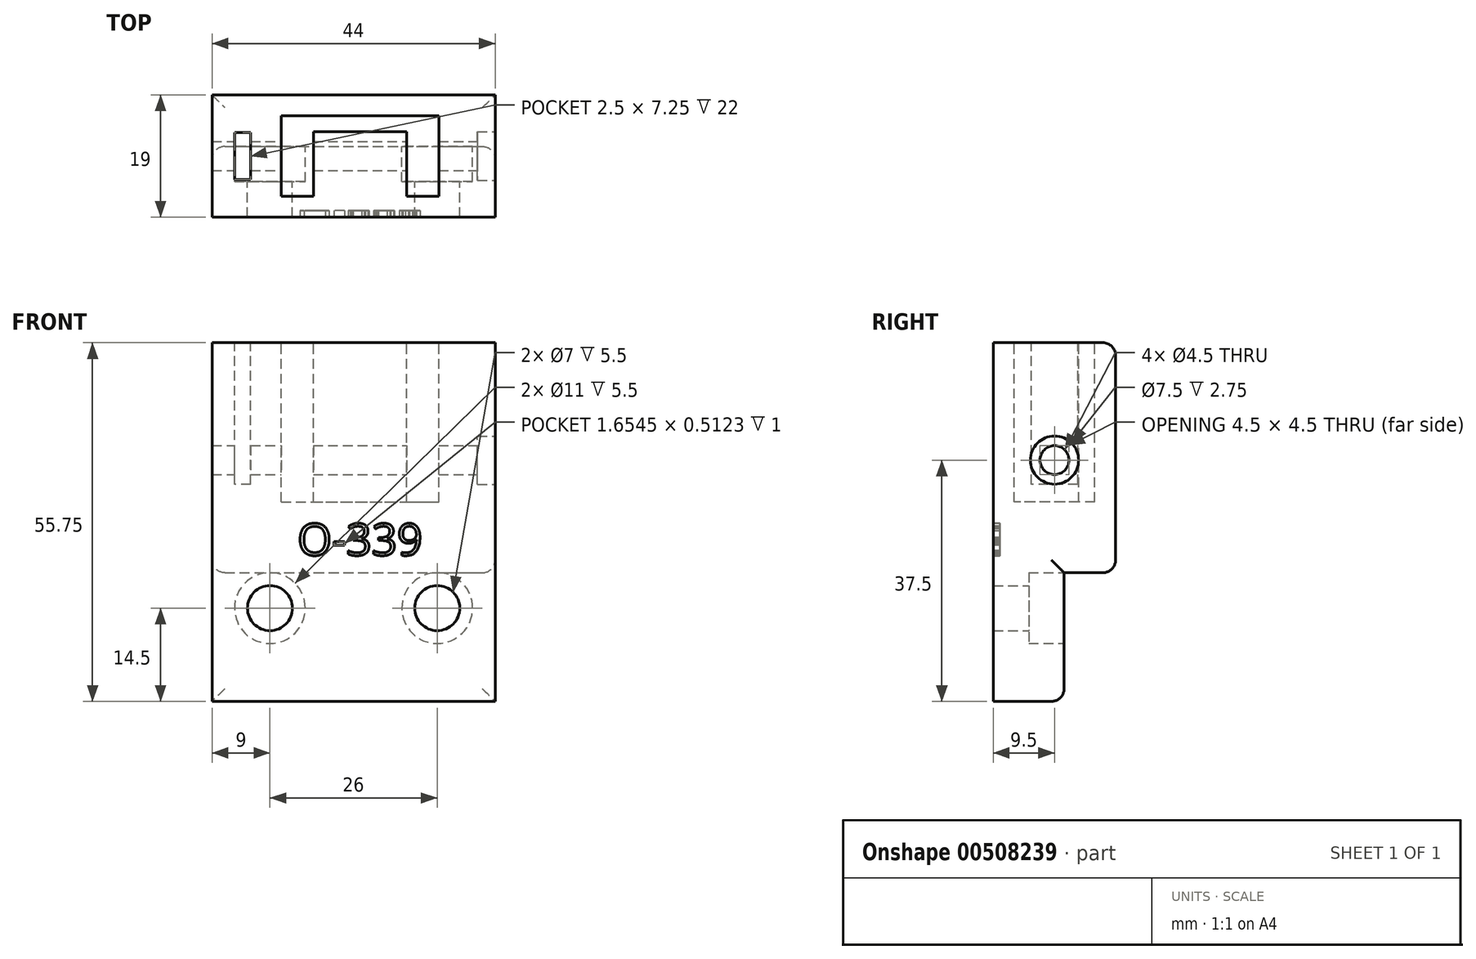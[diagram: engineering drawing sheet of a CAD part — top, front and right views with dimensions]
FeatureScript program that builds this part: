
annotation { "Feature Type Name" : "Feature", "Feature Type Description" : "" }
export const myFeature = defineFeature(function(context is Context, id is Id, definition is map)
    precondition{}
    {
        {
            var Q0;
            Q0=qCreatedBy(makeId("Top.planeOp"),FACE);
            var sketch = newSketch(context, id + "F0", { "sketchPlane" : qUnion([Q0])});
            skLineSegment(sketch, "E0.bottom", {"start": v(-29, 9.5) * mm, "end": v(29, 9.5) * mm});
            skLineSegment(sketch, "E0.top", {"start": v(-29, -9.5) * mm, "end": v(29, -9.5) * mm});
            skLineSegment(sketch, "E0.left", {"start": v(-29, 9.5) * mm, "end": v(-29, -9.5) * mm});
            skLineSegment(sketch, "E0.right", {"start": v(29, 9.5) * mm, "end": v(29, -9.5) * mm});
            skSolve(sketch);
        }
        {
            var Q0;
            Q0=qSketchRegion(id+"F0",true);
            extrude(context, id + "F1", {"entities" : qUnion([Q0]), "depth" : 11 * mm});
        }
        {
            var Q0;
            Q0=makeQuery(id+"F1.opExtrude","CAP_FACE",FACE,{"disambiguationData":[OSD([sQuery(id+"F0.wireOp",EDGE,"E0.bottom"),sQuery(id+"F0.wireOp",EDGE,"E0.top"),sQuery(id+"F0.wireOp",EDGE,"E0.left"),sQuery(id+"F0.wireOp",EDGE,"E0.right"),sQuery(id+"F0.wireOp",EDGE,"AuSHMrTt-jpj0-5Ru2-xaIe-a4Oixfi13iDE"),sQuery(id+"F0.wireOp",EDGE,"9J5HWsQ0-lQpk-E1t6-wWkI-SOKKZm0BYfsw"),sQuery(id+"F0.wireOp",EDGE,"2GzKSPJo-uI2N-Esed-kJXd-WJqO7sIm6bVz"),sQuery(id+"F0.wireOp",EDGE,"DJKESrdY-mQTo-sUHj-6MfV-pHmhVGQO2tIG")])],"isStart":false});
            var sketch = newSketch(context, id + "F2", { "sketchPlane" : qUnion([Q0])});
            skLineSegment(sketch, "E1.bottom", {"start": v(-29, 9.5) * mm, "end": v(29, 9.5) * mm});
            skLineSegment(sketch, "E1.top", {"start": v(-29, -9.5) * mm, "end": v(29, -9.5) * mm});
            skLineSegment(sketch, "E1.left", {"start": v(-29, 9.5) * mm, "end": v(-29, -9.5) * mm});
            skLineSegment(sketch, "E1.right", {"start": v(29, 9.5) * mm, "end": v(29, -9.5) * mm});
            skPoint(sketch, "E1.middle", {"position": v(0, 0) * mm});
            skSolve(sketch);
        }
        {
            var Q0;
            Q0=qSketchRegion(id+"F2",true);
            extrude(context, id + "F3", {"entities" : qUnion([Q0]), "operationType" : NewBodyOperationType.ADD, "depth" : 24.75 * mm});
        }
        {
            var Q0;
            Q0=makeQuery(id+"F3.opExtrude","CAP_FACE",FACE,{"disambiguationData":[OSD([sQuery(id+"F2.wireOp",EDGE,"E1.bottom"),sQuery(id+"F2.wireOp",EDGE,"E1.top"),sQuery(id+"F2.wireOp",EDGE,"E1.left"),sQuery(id+"F2.wireOp",EDGE,"E1.right")])],"isStart":false});
            var sketch = newSketch(context, id + "F4", { "sketchPlane" : qUnion([Q0])});
            skLineSegment(sketch, "E2.bottom", {"start": v(-12.25, 6.25) * mm, "end": v(-7.25, 6.25) * mm});
            skLineSegment(sketch, "E2.top", {"start": v(-12.25, -6.25) * mm, "end": v(-7.25, -6.25) * mm});
            skLineSegment(sketch, "E2.left", {"start": v(-12.25, 6.25) * mm, "end": v(-12.25, -6.25) * mm});
            skLineSegment(sketch, "E2.right", {"start": v(-7.25, 6.25) * mm, "end": v(-7.25, -6.25) * mm});
            skPoint(sketch, "E2.middle", {"position": v(-9.75, 0) * mm});
            skLineSegment(sketch, "E3.bottom", {"start": v(7.25, 6.25) * mm, "end": v(12.25, 6.25) * mm});
            skLineSegment(sketch, "E3.top", {"start": v(7.25, -6.25) * mm, "end": v(12.25, -6.25) * mm});
            skLineSegment(sketch, "E3.left", {"start": v(7.25, 6.25) * mm, "end": v(7.25, -6.25) * mm});
            skLineSegment(sketch, "E3.right", {"start": v(12.25, 6.25) * mm, "end": v(12.25, -6.25) * mm});
            skPoint(sketch, "E3.middle", {"position": v(9.75, 0) * mm});
            skSolve(sketch);
        }
        {
            var Q0;
            Q0=qSketchRegion(id+"F4",true);
            extrude(context, id + "F5", {"entities" : qUnion([Q0]), "operationType" : NewBodyOperationType.REMOVE, "oppositeDirection" : true, "depth" : 24.75 * mm});
        }
        {
            var Q0;
            Q0=makeQuery(id+"F3.boolean.opBoolean","MERGE",FACE,{"derivedFrom":[makeQuery(id+"F1.opExtrude","SWEPT_FACE",FACE,{"disambiguationData":[OSD([sQuery(id+"F0.wireOp",EDGE,"E0.right")])]}),makeQuery(id+"F3.opExtrude","SWEPT_FACE",FACE,{"disambiguationData":[OSD([sQuery(id+"F2.wireOp",EDGE,"E1.right")])]})]});
            var sketch = newSketch(context, id + "F6", { "sketchPlane" : qUnion([Q0])});
            skCircle(sketch, "E4", {"center": v(0, 17.5) * mm, "radius": 2.25 * mm});
            skSolve(sketch);
        }
        {
            var Q0;
            Q0=qSketchRegion(id+"F6",true);
            extrude(context, id + "F7", {"entities" : qUnion([Q0]), "operationType" : NewBodyOperationType.REMOVE, "endBound" : BoundingType.THROUGH_ALL, "oppositeDirection" : true, "depth" : 53 * mm});
        }
        {
            var Q0;
            Q0=makeQuery(id+"F3.opExtrude","CAP_FACE",FACE,{"disambiguationData":[OSD([sQuery(id+"F2.wireOp",EDGE,"E1.bottom"),sQuery(id+"F2.wireOp",EDGE,"E1.top"),sQuery(id+"F2.wireOp",EDGE,"E1.left"),sQuery(id+"F2.wireOp",EDGE,"E1.right")])],"isStart":false});
            var sketch = newSketch(context, id + "F8", { "sketchPlane" : qUnion([Q0])});
            skLineSegment(sketch, "E5.bottom", {"start": v(-7.25, 6.25) * mm, "end": v(7.25, 6.25) * mm});
            skLineSegment(sketch, "E5.top", {"start": v(-7.25, 3.75) * mm, "end": v(7.25, 3.75) * mm});
            skLineSegment(sketch, "E5.left", {"start": v(-7.25, 6.25) * mm, "end": v(-7.25, 3.75) * mm});
            skLineSegment(sketch, "E5.right", {"start": v(7.25, 6.25) * mm, "end": v(7.25, 3.75) * mm});
            skSolve(sketch);
        }
        {
            var Q0;
            Q0=qSketchRegion(id+"F8",true);
            extrude(context, id + "F9", {"entities" : qUnion([Q0]), "operationType" : NewBodyOperationType.REMOVE, "oppositeDirection" : true, "depth" : 24.75 * mm});
        }
        {
            var Q0;
            Q0=makeQuery(id+"F3.boolean.opBoolean","MERGE",FACE,{"derivedFrom":[makeQuery(id+"F1.opExtrude","SWEPT_FACE",FACE,{"disambiguationData":[OSD([sQuery(id+"F0.wireOp",EDGE,"E0.right")])]}),makeQuery(id+"F3.opExtrude","SWEPT_FACE",FACE,{"disambiguationData":[OSD([sQuery(id+"F2.wireOp",EDGE,"E1.right")])]})]});
            var sketch = newSketch(context, id + "F10", { "sketchPlane" : qUnion([Q0])});
            skCircle(sketch, "E6", {"center": v(0, 17.5) * mm, "radius": 3.75 * mm});
            skSolve(sketch);
        }
        {
            var Q0;
            Q0=qSketchRegion(id+"F10",true);
            extrude(context, id + "F11", {"entities" : qUnion([Q0]), "operationType" : NewBodyOperationType.REMOVE, "oppositeDirection" : true, "depth" : 10.75 * mm});
        }
        {
            var Q0;
            Q0=makeQuery(id+"F3.opExtrude","CAP_FACE",FACE,{"disambiguationData":[OSD([sQuery(id+"F2.wireOp",EDGE,"E1.bottom"),sQuery(id+"F2.wireOp",EDGE,"E1.top"),sQuery(id+"F2.wireOp",EDGE,"E1.left"),sQuery(id+"F2.wireOp",EDGE,"E1.right")])],"isStart":false});
            var sketch = newSketch(context, id + "F12", { "sketchPlane" : qUnion([Q0])});
            skLineSegment(sketch, "E7.bottom", {"start": v(-17, 3.63) * mm, "end": v(-19.5, 3.63) * mm});
            skLineSegment(sketch, "E7.top", {"start": v(-17, -3.62) * mm, "end": v(-19.5, -3.62) * mm});
            skLineSegment(sketch, "E7.left", {"start": v(-17, 3.63) * mm, "end": v(-17, -3.62) * mm});
            skLineSegment(sketch, "E7.right", {"start": v(-19.5, 3.63) * mm, "end": v(-19.5, -3.62) * mm});
            skPoint(sketch, "E7.middle", {"position": v(-18.25, 0) * mm});
            skSolve(sketch);
        }
        {
            var Q0;
            Q0=qSketchRegion(id+"F12",true);
            extrude(context, id + "F13", {"entities" : qUnion([Q0]), "operationType" : NewBodyOperationType.REMOVE, "oppositeDirection" : true, "depth" : 22 * mm});
        }
        {
            var Q0;
            Q0=makeQuery(id+"F1.opExtrude","SWEPT_FACE",FACE,{"disambiguationData":[OSD([sQuery(id+"F0.wireOp",EDGE,"E0.top")])]});
            var sketch = newSketch(context, id + "F14", { "sketchPlane" : qUnion([Q0])});
            skText(sketch, "E8", { "text": "O-339", "fontName": "OpenSans-Regular.ttf"});
            const initialGuessF14  = {"E8": [-0.00974, 0.0027, 1, 0, 0.00497]};
            skSetInitialGuess(sketch, initialGuessF14);
            skSolve(sketch);
        }
        {
            var Q0;
            Q0=qSketchRegion(id+"F14",true);
            extrude(context, id + "F15", {"entities" : qUnion([Q0]), "operationType" : NewBodyOperationType.REMOVE, "oppositeDirection" : true, "depth" : 1 * mm});
        }
        {
            var Q0;
            {var subQ1=sQuery(id+"F0.wireOp",EDGE,"E0.left");var subQ2=sQuery(id+"F0.wireOp",EDGE,"E0.top");var subQ5=sQuery(id+"F2.wireOp",EDGE,"E1.top");Q0=makeQuery(id+"FO3PEAp2ygwaakO_1.boolean.opBoolean","MERGE",FACE,{"derivedFrom":[makeQuery(id+"F15.boolean.opBoolean","SPLIT",FACE,{"disambiguationData":[TD([makeQuery(id+"F1.opExtrude","SWEPT_FACE",FACE,{"disambiguationData":[OSD([subQ1])]})])],"derivedFrom":makeQuery(id+"F3.boolean.opBoolean","MERGE",FACE,{"derivedFrom":[makeQuery(id+"F1.opExtrude","SWEPT_FACE",FACE,{"disambiguationData":[OSD([subQ2])]}),makeQuery(id+"F3.opExtrude","SWEPT_FACE",FACE,{"disambiguationData":[OSD([subQ5])]})]})}),makeQuery(id+"FO3PEAp2ygwaakO_1.opExtrude","SWEPT_FACE",FACE,{"disambiguationData":[OSD([sQuery(id+"F4FtiOInvpE9sW0_1.wireOp",EDGE,"hhqaLyYQ-Ikl1-l38m-BBv7-oSqBDNAxtoTe")])]})]});}
            var sketch = newSketch(context, id + "F16", { "sketchPlane" : qUnion([Q0])});
            skLineSegment(sketch, "E9.bottom", {"start": v(-29, 0) * mm, "end": v(29, 0) * mm});
            skLineSegment(sketch, "E9.top", {"start": v(-29, -20) * mm, "end": v(29, -20) * mm});
            skLineSegment(sketch, "E9.left", {"start": v(-29, 0) * mm, "end": v(-29, -20) * mm});
            skLineSegment(sketch, "E9.right", {"start": v(29, 0) * mm, "end": v(29, -20) * mm});
            skSolve(sketch);
        }
        {
            var Q0;
            Q0=qSketchRegion(id+"F16",true);
            extrude(context, id + "F17", {"entities" : qUnion([Q0]), "operationType" : NewBodyOperationType.ADD, "oppositeDirection" : true, "depth" : 11 * mm});
        }
        {
            var Q0;
            Q0=makeQuery(id+"F17.opExtrude","CAP_FACE",FACE,{"disambiguationData":[OSD([sQuery(id+"F16.wireOp",EDGE,"E9.bottom"),sQuery(id+"F16.wireOp",EDGE,"E9.top"),sQuery(id+"F16.wireOp",EDGE,"E9.left"),sQuery(id+"F16.wireOp",EDGE,"E9.right")])],"isStart":false});
            var sketch = newSketch(context, id + "F18", { "sketchPlane" : qUnion([Q0])});
            skCircle(sketch, "E10", {"center": v(-12, -5.5) * mm, "radius": 3.5 * mm});
            skCircle(sketch, "E11", {"center": v(14, -5.5) * mm, "radius": 3.5 * mm});
            skSolve(sketch);
        }
        {
            var Q0;
            Q0=qSketchRegion(id+"F18",true);
            extrude(context, id + "F19", {"entities" : qUnion([Q0]), "operationType" : NewBodyOperationType.REMOVE, "endBound" : BoundingType.THROUGH_ALL, "oppositeDirection" : true, "depth" : 25 * mm});
        }
        {
            var Q0;
            Q0=makeQuery(id+"F17.opExtrude","CAP_FACE",FACE,{"disambiguationData":[OSD([sQuery(id+"F16.wireOp",EDGE,"E9.bottom"),sQuery(id+"F16.wireOp",EDGE,"E9.top"),sQuery(id+"F16.wireOp",EDGE,"E9.left"),sQuery(id+"F16.wireOp",EDGE,"E9.right")])],"isStart":false});
            var sketch = newSketch(context, id + "F20", { "sketchPlane" : qUnion([Q0])});
            skCircle(sketch, "E12", {"center": v(-12, -5.5) * mm, "radius": 5.5 * mm});
            skCircle(sketch, "E13", {"center": v(14, -5.5) * mm, "radius": 5.5 * mm});
            skSolve(sketch);
        }
        {
            var Q0;
            Q0=qSketchRegion(id+"F20",true);
            extrude(context, id + "F21", {"entities" : qUnion([Q0]), "operationType" : NewBodyOperationType.REMOVE, "oppositeDirection" : true, "depth" : 5.5 * mm});
        }
        {
            var Q0;
            Q0=makeQuery(id+"F3.boolean.opBoolean","MERGE",FACE,{"derivedFrom":[makeQuery(id+"F1.opExtrude","SWEPT_FACE",FACE,{"disambiguationData":[OSD([sQuery(id+"F0.wireOp",EDGE,"E0.bottom")])]}),makeQuery(id+"F3.opExtrude","SWEPT_FACE",FACE,{"disambiguationData":[OSD([sQuery(id+"F2.wireOp",EDGE,"E1.bottom")])]})]});
            var sketch = newSketch(context, id + "F22", { "sketchPlane" : qUnion([Q0])});
            skLineSegment(sketch, "E14.bottom", {"start": v(-29, 35.75) * mm, "end": v(-21, 35.75) * mm});
            skLineSegment(sketch, "E14.top", {"start": v(-29, -20) * mm, "end": v(-21, -20) * mm});
            skLineSegment(sketch, "E14.left", {"start": v(-29, 35.75) * mm, "end": v(-29, -20) * mm});
            skLineSegment(sketch, "E15.bottom", {"start": v(29, 35.75) * mm, "end": v(23, 35.75) * mm});
            skLineSegment(sketch, "E15.top", {"start": v(29, -20) * mm, "end": v(23, -20) * mm});
            skLineSegment(sketch, "E15.left", {"start": v(29, 35.75) * mm, "end": v(29, -20) * mm});
            skLineSegment(sketch, "E15.right", {"start": v(23, 35.75) * mm, "end": v(23, -20) * mm});
            skLineSegment(sketch, "E16", {"start": v(-21, 35.75) * mm, "end": v(-21, -20) * mm});
            skSolve(sketch);
        }
        {
            var Q0;
            Q0 = qSketchRegion(id + "F22", true);
            extrude(context, id + "F23", {"entities" : qUnion([Q0]), "operationType" : NewBodyOperationType.REMOVE, "endBound" : BoundingType.THROUGH_ALL, "oppositeDirection" : true, "depth" : 25 * mm});
        }
        {
            var Q0;
            Q0=makeQuery(id+"F23.boolean.opBoolean","INTERSECT",EDGE,{"derivedFrom":[makeQuery(id+"F17.opExtrude","CAP_FACE",FACE,{"disambiguationData":[OSD([sQuery(id+"F16.wireOp",EDGE,"E9.bottom"),sQuery(id+"F16.wireOp",EDGE,"E9.top"),sQuery(id+"F16.wireOp",EDGE,"E9.left"),sQuery(id+"F16.wireOp",EDGE,"E9.right")])],"isStart":false}),makeQuery(id+"F23.opExtrude","SWEPT_FACE",FACE,{"disambiguationData":[OSD([sQuery(id+"F22.wireOp",EDGE,"E16")])]})]});
            var Q1;
            Q1=makeQuery(id+"F17.opExtrude","CAP_EDGE",EDGE,{"disambiguationData":[OSD([sQuery(id+"F16.wireOp",EDGE,"E9.top")])],"isStart":false});
            var Q2;
            Q2=makeQuery(id+"F23.boolean.opBoolean","COPY",EDGE,{"derivedFrom":makeQuery(id+"F23.opExtrude","SWEPT_EDGE",EDGE,{"disambiguationData":[OSD([sQuery(id+"F22.wireOp",EDGE,"E14.top"),sQuery(id+"F22.wireOp",EDGE,"E16")])]})});
            var Q3;
            Q3=makeQuery(id+"F23.boolean.opBoolean","INTERSECT",EDGE,{"derivedFrom":[makeQuery(id+"F1.opExtrude","CAP_FACE",FACE,{"disambiguationData":[OSD([sQuery(id+"F0.wireOp",EDGE,"E0.bottom"),sQuery(id+"F0.wireOp",EDGE,"E0.top"),sQuery(id+"F0.wireOp",EDGE,"E0.left"),sQuery(id+"F0.wireOp",EDGE,"E0.right")])],"isStart":true}),makeQuery(id+"F23.opExtrude","SWEPT_FACE",FACE,{"disambiguationData":[OSD([sQuery(id+"F22.wireOp",EDGE,"E16")])]})]});
            var Q4;
            Q4=makeQuery(id+"F23.boolean.opBoolean","COPY",EDGE,{"derivedFrom":makeQuery(id+"F23.opExtrude","CAP_EDGE",EDGE,{"disambiguationData":[OSD([sQuery(id+"F22.wireOp",EDGE,"E16")])],"isStart":true})});
            var Q5;
            Q5=makeQuery(id+"F1.opExtrude","CAP_EDGE",EDGE,{"disambiguationData":[OSD([sQuery(id+"F0.wireOp",EDGE,"E0.bottom")])],"isStart":true});
            var Q6;
            Q6=makeQuery(id+"F23.boolean.opBoolean","INTERSECT",EDGE,{"derivedFrom":[makeQuery(id+"F17.opExtrude","CAP_FACE",FACE,{"disambiguationData":[OSD([sQuery(id+"F16.wireOp",EDGE,"E9.bottom"),sQuery(id+"F16.wireOp",EDGE,"E9.top"),sQuery(id+"F16.wireOp",EDGE,"E9.left"),sQuery(id+"F16.wireOp",EDGE,"E9.right")])],"isStart":false}),makeQuery(id+"F23.opExtrude","SWEPT_FACE",FACE,{"disambiguationData":[OSD([sQuery(id+"F22.wireOp",EDGE,"E15.right")])]})]});
            var Q7;
            Q7=makeQuery(id+"F23.boolean.opBoolean","COPY",EDGE,{"derivedFrom":makeQuery(id+"F23.opExtrude","SWEPT_EDGE",EDGE,{"disambiguationData":[OSD([sQuery(id+"F22.wireOp",EDGE,"E15.top"),sQuery(id+"F22.wireOp",EDGE,"E15.right")])]})});
            var Q8;
            Q8=makeQuery(id+"F23.boolean.opBoolean","INTERSECT",EDGE,{"derivedFrom":[makeQuery(id+"F1.opExtrude","CAP_FACE",FACE,{"disambiguationData":[OSD([sQuery(id+"F0.wireOp",EDGE,"E0.bottom"),sQuery(id+"F0.wireOp",EDGE,"E0.top"),sQuery(id+"F0.wireOp",EDGE,"E0.left"),sQuery(id+"F0.wireOp",EDGE,"E0.right")])],"isStart":true}),makeQuery(id+"F23.opExtrude","SWEPT_FACE",FACE,{"disambiguationData":[OSD([sQuery(id+"F22.wireOp",EDGE,"E15.right")])]})]});
            var Q9;
            Q9=makeQuery(id+"F23.boolean.opBoolean","COPY",EDGE,{"derivedFrom":makeQuery(id+"F23.opExtrude","CAP_EDGE",EDGE,{"disambiguationData":[OSD([sQuery(id+"F22.wireOp",EDGE,"E15.right")])],"isStart":true})});
            var Q10;
            Q10=makeQuery(id+"F3.opExtrude","CAP_EDGE",EDGE,{"disambiguationData":[OSD([sQuery(id+"F2.wireOp",EDGE,"E1.bottom")])],"isStart":false});
            var Q11;
            Q11=makeQuery(id+"F23.boolean.opBoolean","COPY",EDGE,{"derivedFrom":makeQuery(id+"F23.opExtrude","SWEPT_EDGE",EDGE,{"disambiguationData":[OSD([sQuery(id+"F2.wireOp",EDGE,"E1.bottom"),sQuery(id+"F22.wireOp",EDGE,"E14.bottom"),sQuery(id+"F22.wireOp",EDGE,"E16")])]})});
            var Q12;
            Q12=makeQuery(id+"F23.boolean.opBoolean","COPY",EDGE,{"derivedFrom":makeQuery(id+"F23.opExtrude","SWEPT_EDGE",EDGE,{"disambiguationData":[OSD([sQuery(id+"F2.wireOp",EDGE,"E1.bottom"),sQuery(id+"F22.wireOp",EDGE,"E15.bottom"),sQuery(id+"F22.wireOp",EDGE,"E15.right")])]})});
            fillet(context, id + "F24", {"entities" : qUnion([Q0, Q1, Q2, Q3, Q4, Q5, Q6, Q7, Q8, Q9, Q10, Q11, Q12]), "radius" : 2 * mm, "tangentPropagation" : true, "allowEdgeOverflow" : false});
        }
    });
